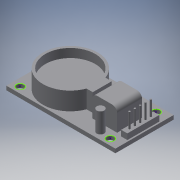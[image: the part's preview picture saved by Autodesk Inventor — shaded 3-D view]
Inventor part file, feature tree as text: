
AUTODESK INVENTOR PART (.ipt)
format: ipt  version: 2016 (Build 200138000, 138)  size: 212,480 bytes
history: native  units: in
note: dims shown in document units (in); Inventor stores cm internally (conversion verified against a paired STEP export)
features: sketch x11, extrude x9, fillet x1
ambient origin geometry x8: Origin, YZ Plane, XZ Plane, XY Plane, X Axis, Y Axis, Z Axis, Center Point
bodies: Solid1 (feature_tree)
feature tree (21):
  extrude  "Extrusion1"  Depth=0.9213in
  extrude  "Extrusion2"  Depth=0.5039in
  extrude  "Extrusion3"  Depth=0.0984in
  extrude  "Extrusion4"  Depth=0.0906in TaperAngle=0.0deg
  extrude  "Extrusion5"  Depth=0.0276in
  extrude  "Extrusion6"  Depth=0.0276in
  sketch  "Sketch7"  dims[d16=0.0276in d17=0.0276in]
  extrude  "Extrusion7"  Depth=0.0276in
  extrude  "Extrusion8"  Depth=0.0839in
  fillet  "Fillet1"  Radius=0.0839in
  extrude  "Extrusion9"  Depth=0.2362in TaperAngle=0.0deg
  sketch  "Sketch12"  dims[d28=0.2835in d29=0.0in d30=0.2992in d31=0.0984in d32=0.0984in d33=0.2835in d34=0.0in d35=0.7874in d36=0.1378in d37=0.0in d38=0.0827in d39=0.3937in d40=0.3937in d41=0.2953in d42=0.3465in d43=0.0in d44=0.5512in d45=0.4606in d46=0.1181in d47=0.3543in d48=0.1181in d49=0.315in d50=0.0in d51=0.0787in d52=0.1181in d53=0.1181in d54=0.8425in d55=0.1181in d56=1.4252in d57=0.1181in d58=0.1181in d59=0.1181in d60=0.7244in d61=0.0984in d62=0.0984in d64=1.4252in d65=0.315in d66=0.0in]
  sketch  "Sketch1"  dims[d0=1.7244in d1=0.9213in]
  sketch  "Sketch2"  dims[d2=0.063in d3=0.0in d6=0.5039in]
  sketch  "Sketch3"  dims[d7=0.0236in d8=0.0984in]
  sketch  "Sketch4"  dims[d9=0.2126in d10=0.0906in d11=0.0in]
  sketch  "Sketch5"  dims[d12=0.0839in d13=0.0276in]
  sketch  "Sketch6"  dims[d14=0.0276in d15=0.0276in]
  sketch  "Sketch8"  dims[d19=0.0839in d20=0.0839in d21=0.0839in]
  sketch  "Sketch10"  dims[d22=0.0839in d23=0.2362in d24=0.0in]
  sketch  "Sketch11"  dims[d25=0.8661in]
